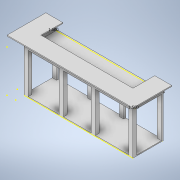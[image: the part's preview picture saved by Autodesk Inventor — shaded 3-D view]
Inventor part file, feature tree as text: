
AUTODESK INVENTOR PART (.ipt)
format: ipt  version: 2020 (Build 240168000, 168)  size: 327,168 bytes
history: native  units: in
note: dims shown in document units (in); Inventor stores cm internally (conversion verified against a paired STEP export)
features: sketch x19, extrude x14
ambient origin geometry x8: Origin, YZ Plane, XZ Plane, XY Plane, X Axis, Y Axis, Z Axis, Center Point
bodies: Solid1 (feature_tree)
feature tree (33):
  extrude  "Extrusion1"  Depth=32.0in
  extrude  "Extrusion2"  Depth=7.0in
  extrude  "Extrusion3"  Depth=7.0in
  extrude  "Extrusion4"  Depth=104.0in TaperAngle=0.0deg
  extrude  "Extrusion5"  Depth=104.0in TaperAngle=0.0deg
  extrude  "Extrusion6"  Depth=0.75in
  sketch  "Sketch8"  dims[d16=1.5in d17=33.0in]
  extrude  "Extrusion7"  Depth=33.0in
  sketch  "Sketch10"  dims[d20=33.0in d21=0.75in]
  sketch  "Sketch11"  dims[d22=104.0in d23=0.0in d25=7.0in]
  extrude  "Extrusion8"  Depth=1.5in
  extrude  "Extrusion9"  Depth=0.75in
  extrude  "Extrusion10"  Depth=7.0in
  extrude  "Extrusion11"  Depth=14.0in
  sketch  "Sketch16"  dims[d35=8.0in d36=0.0in]
  extrude  "Extrusion12"  Depth=14.0in
  extrude  "Extrusion13"  Depth=1.5in
  extrude  "Extrusion14"  Depth=1.5in
  sketch  "Sketch22"  dims[d43=1.0in d44=0.0in d45=1.0in d46=0.0in d47=1.0in d48=0.0in d49=1.0in d50=0.0in d51=1.5in d52=1.5in d53=0.75in d54=0.0in d58=1.0in d59=33.0in d60=150.0in d61=0.0in d72=3.5in d73=27.5in d74=33.0in d75=3.5in d76=23.0in d77=33.0in d78=3.5in d79=33.0in d80=3.5in d81=33.0in d82=3.0in d83=0.0in d84=1.5in d85=0.0344in]
  sketch  "Sketch1"  dims[d0=43.0in d1=32.0in]
  sketch  "Sketch2"  dims[d2=104.0in d3=0.0in d4=7.0in]
  sketch  "Sketch3"  dims[d5=42.25in d6=7.0in]
  sketch  "Sketch4"  dims[d7=42.25in d8=104.0in d9=0.0in]
  sketch  "Sketch6"  dims[d10=7.0in d11=104.0in d12=0.0in]
  sketch  "Sketch7"  dims[d13=25.0in d15=0.75in]
  sketch  "Sketch9"  dims[d18=24.0in d19=1.5in]
  sketch  "Sketch12"  dims[d26=7.0in d27=14.0in]
  sketch  "Sketch13"  dims[d28=18.0in d29=14.0in]
  sketch  "Sketch14"  dims[d30=1.0in d31=0.0in d32=1.5in]
  sketch  "Sketch15"  dims[d33=1.5in d34=1.5in]
  sketch  "Sketch17"  dims[d38=0.75in]
  sketch  "Sketch18"  dims[d39=90.0in]
  sketch  "Sketch21"  dims[d40=1.0in d41=0.0in]
